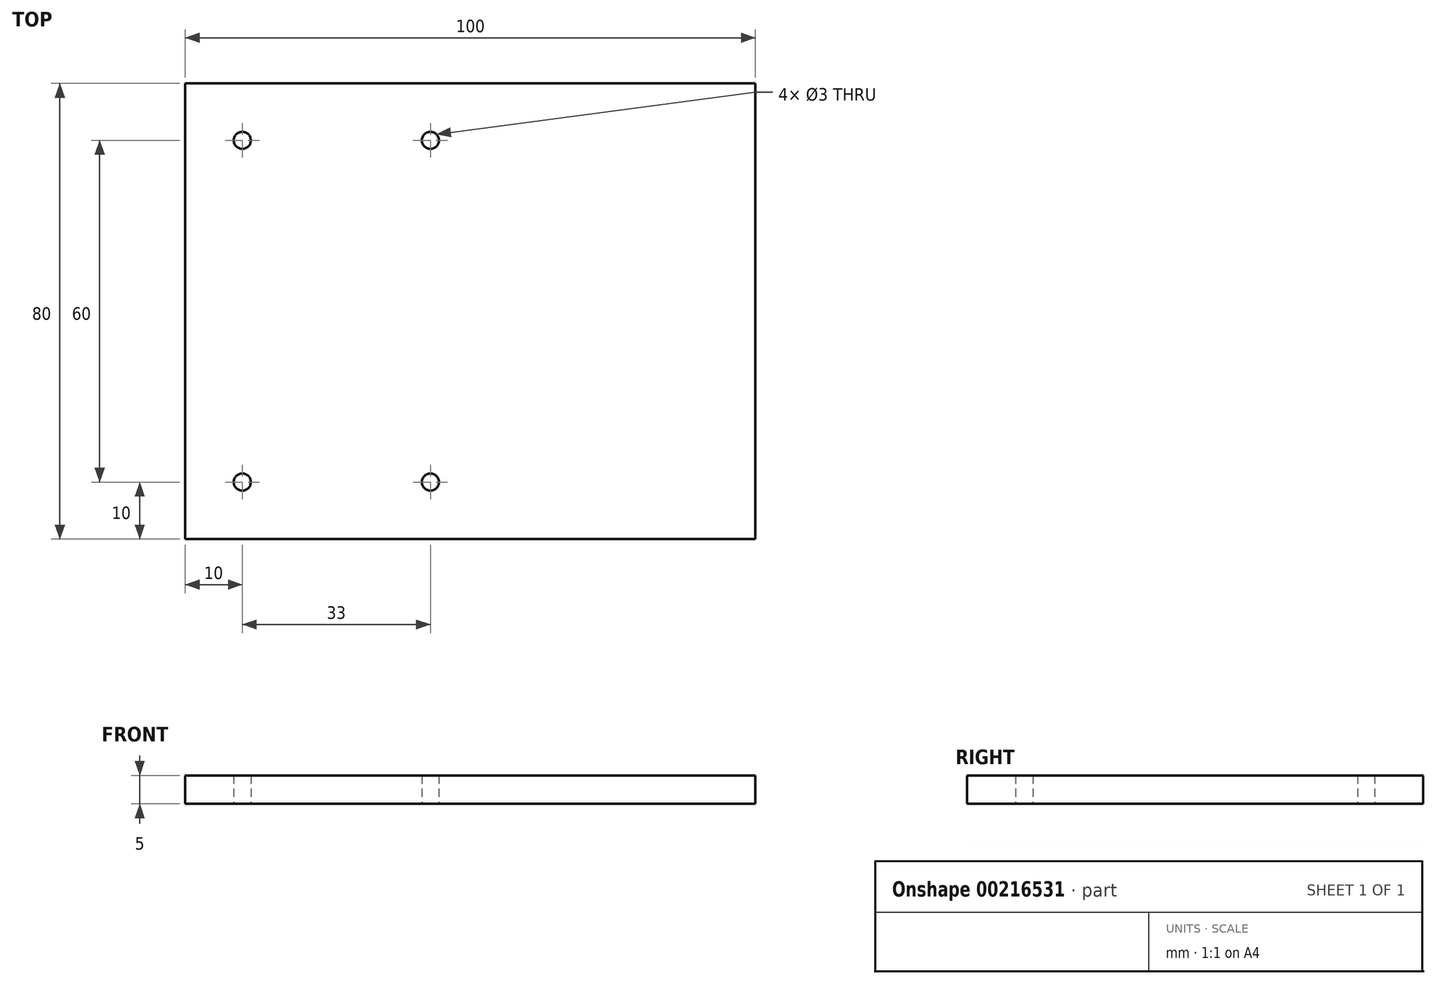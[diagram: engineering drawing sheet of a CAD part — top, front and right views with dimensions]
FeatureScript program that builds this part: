
annotation { "Feature Type Name" : "Feature", "Feature Type Description" : "" }
export const myFeature = defineFeature(function(context is Context, id is Id, definition is map)
    precondition{}
    {
        {
            var Q0;
            Q0=qCreatedBy(makeId("Top.planeOp"),FACE);
            var sketch = newSketch(context, id + "F0", { "sketchPlane" : qUnion([Q0])});
            skLineSegment(sketch, "E0.bottom", {"start": v(-50, 40) * mm, "end": v(50, 40) * mm});
            skLineSegment(sketch, "E0.top", {"start": v(-50, -40) * mm, "end": v(50, -40) * mm});
            skLineSegment(sketch, "E0.left", {"start": v(-50, 40) * mm, "end": v(-50, -40) * mm});
            skLineSegment(sketch, "E0.right", {"start": v(50, 40) * mm, "end": v(50, -40) * mm});
            skCircle(sketch, "E1", {"center": v(-40, 30) * mm, "radius": 1.5 * mm});
            skCircle(sketch, "E2.0.1.0", {"center": v(-40, -30) * mm, "radius": 1.5 * mm});
            skCircle(sketch, "E2.1.0.0", {"center": v(-7, 30) * mm, "radius": 1.5 * mm});
            skCircle(sketch, "E2.1.1.0", {"center": v(-7, -30) * mm, "radius": 1.5 * mm});
            skLineSegment(sketch, "E2.direction1", {"start": v(-40, 30) * mm, "end": v(-7, 30) * mm, "construction": true});
            skLineSegment(sketch, "E2.direction2", {"start": v(-40, 30) * mm, "end": v(-40, -30) * mm, "construction": true});
            skSolve(sketch);
        }
        {
            var Q0;
            Q0=makeQuery(id+"F0.imprint","IMPRINT",FACE,{"disambiguationData":[TD([[makeQuery(id+"F0.imprint","IMPRINT",EDGE,{"derivedFrom":sQuery(id+"F0.wireOp",EDGE,"E0.bottom")}),-1.0]])]});
            extrude(context, id + "F1", {"entities" : qUnion([Q0]), "depth" : 5 * mm});
        }
    });
